FCSTD DOCUMENT  (FreeCAD 0.16R6223 (Git))
Label: map2_smd_assy
License: All rights reserved
LicenseURL: http://en.wikipedia.org/wiki/All_rights_reserved
objects: Part::Feature×12, Part::FeaturePython×7, Sketcher::SketchObject×2, PartDesign::Pad×2, Part::MultiFuse×2
note: 27 computed .brp shape members not serialized (recipe doc carries the construction recipe); baked Part::Feature solids carry a one-line shape summary decoded from their .brp

FEATURE [Sketcher::SketchObject] Sketch
  sketch-geometry (4):
    g0: LineSegment StartX=0 StartY=0 StartZ=0 EndX=132.08 EndY=0 EndZ=0
    g1: LineSegment StartX=132.08 StartY=0 StartZ=0 EndX=132.08 EndY=127 EndZ=0
    g2: LineSegment StartX=132.08 StartY=127 StartZ=0 EndX=0 EndY=127 EndZ=0
    g3: LineSegment StartX=0 StartY=127 StartZ=0 EndX=0 EndY=0 EndZ=0
  constraints (11):
    c: Coincident(g0,g1)
    c: Coincident(g1,g2)
    c: Coincident(g2,g3)
    c: Coincident(g3,g0)
    c: Horizontal(g0)
    c: Horizontal(g2)
    c: Vertical(g1)
    c: Vertical(g3)
    c: DistanceX(g2) = -132.08
    c: DistanceY(g3) = -127
    c: Coincident(g0,g-1)
FEATURE [PartDesign::Pad] Pad
  Length = 6.35
  Length2 = 100
  Reversed = true
  Sketch = -> Sketch
  Type = 0
FEATURE [Sketcher::SketchObject] Sketch001
  sketch-geometry (4):
    g0: LineSegment StartX=1.27 StartY=127 StartZ=0 EndX=6.35 EndY=127 EndZ=0
    g1: LineSegment StartX=6.35 StartY=127 StartZ=0 EndX=6.35 EndY=0 EndZ=0
    g2: LineSegment StartX=6.35 StartY=0 StartZ=0 EndX=1.27 EndY=0 EndZ=0
    g3: LineSegment StartX=1.27 StartY=0 StartZ=0 EndX=1.27 EndY=127 EndZ=0
  constraints (12):
    c: Coincident(g0,g1)
    c: Coincident(g1,g2)
    c: Coincident(g2,g3)
    c: Coincident(g3,g0)
    c: Horizontal(g0)
    c: Horizontal(g2)
    c: Vertical(g1)
    c: Vertical(g3)
    c: DistanceY(g3) = 127
    c: DistanceX(g0) = 5.08
    c: DistanceY(g-1,g2) = 0
    c: DistanceX(g-1,g2) = 1.27
FEATURE [PartDesign::Pad] Pad001
  Length = 0.254
  Length2 = 100
  Sketch = -> Sketch001
  Type = 0
FEATURE [Part::FeaturePython] Array  # Draft array (typed FeaturePython)
  Angle = 360
  ArrayType = 0
  Axis = (0,0,1)
  Base = -> Pad001
  Center = (0,0,0)
  Fuse = false
  IntervalAxis = (0,0,0)
  IntervalX = (25.4,0,0)
  IntervalY = (0,0,0)
  IntervalZ = (0,0,0)
  NumberPolar = 1
  NumberX = 6
  NumberY = 2
  NumberZ = 1
  Placement = pos=(2.54,0,0) rot=(0,0,1;0rad)
FEATURE [Part::Feature] Pcb
  Placement = pos=(-45.72,45.72,0) rot=(0,0,1;0rad)
  shape: bbox 25.4 x 25.4 x 1.6 mm, 76 faces (baked)
FEATURE [Part::Feature] Shape  label="R_photo_"
  Placement = pos=(0,-1.27,0) rot=(0,0,-1;1.5708rad)
  shape: bbox 4.775 x 5.625 x 3.889 mm, 86 faces (baked)
FEATURE [Part::Feature] Shape001  label="Fusion_"
  Placement = pos=(0,5.715,0) rot=(0,0,-1;1.5708rad)
  shape: bbox 6.02 x 5.42 x 14.8 mm, 87 faces (baked)
FEATURE [Part::Feature] Shape002  label="Tr_SOT23_"
  Placement = pos=(-8.382,9.906,0) rot=(0,0,1;3.14159rad)
  shape: bbox 2.9 x 2.3 x 1 mm, 217 faces (baked)
FEATURE [Part::Feature] Shape003  label="r_0805_"
  Placement = pos=(0,-6.35,0) rot=(0,0,1;3.14159rad)
  shape: bbox 2 x 1.25 x 0.782 mm, 90 faces (baked)
FEATURE [Part::Feature] Shape004  label="r_0805_001"
  Placement = pos=(4.445,3.81,0) rot=(0,0,-1;1.5708rad)
  shape: bbox 1.25 x 2 x 0.782 mm, 90 faces (baked)
FEATURE [Part::Feature] Shape005  label="r_0805_002"
  Placement = pos=(0,10.16,0) rot=(0,0,1;0rad)
  shape: bbox 2 x 1.25 x 0.782 mm, 90 faces (baked)
FEATURE [Part::Feature] Shape006  label="r_0805_003"
  Placement = pos=(-4.445,3.81,0) rot=(0,0,-1;1.5708rad)
  shape: bbox 1.25 x 2 x 0.782 mm, 90 faces (baked)
FEATURE [Part::Feature] Shape007  label="cap_1210_3225M_"
  Placement = pos=(-8.255,-2.54,0) rot=(0,0,1;3.14159rad)
  shape: bbox 4.001 x 2.489 x 1.704 mm, 108 faces (baked)
FEATURE [Part::Feature] Shape008  label="cap_1210_3225M_001"
  Placement = pos=(8.255,-2.54,0) rot=(0,0,1;3.14159rad)
  shape: bbox 4.001 x 2.489 x 1.704 mm, 108 faces (baked)
FEATURE [Part::Feature] Shape009  label="cap_1210_3225M_002"
  Placement = pos=(8.89,8.89,0) rot=(0,0,1;3.14159rad)
  shape: bbox 4.001 x 2.489 x 1.704 mm, 108 faces (baked)
FEATURE [Part::MultiFuse] Fusion
  Shapes = -> [Shape,Shape001,Shape002,Shape003,Shape004,Shape005,Shape006,Shape007,Shape008,Shape009,Pcb]
FEATURE [Part::Feature] Part__Feature_solid  label="header_1x2_TH_2_54mm078 (Solid)"
  shape: bbox 2.54 x 5.08 x 12.7 mm, 78 faces (baked)
FEATURE [Part::FeaturePython] Clone  label="Clone of header_1x2_TH_2_54mm078 (Solid)"  # Draft clone (typed FeaturePython)
  Objects = -> [Part__Feature_solid]
  Placement = pos=(-25.4,0,0) rot=(0,0,1;0rad)
  Scale = (1,1,1)
FEATURE [Part::MultiFuse] Fusion001
  Placement = pos=(19.05,25.4,11.43) rot=(0,0,1;0rad)
  Shapes = -> [Fusion,Part__Feature_solid,Clone]
FEATURE [Part::FeaturePython] Array001  # Draft array (typed FeaturePython)
  Angle = 360
  ArrayType = 0
  Axis = (0,0,1)
  Base = -> Fusion001
  Center = (0,0,0)
  Fuse = false
  IntervalAxis = (0,0,0)
  IntervalX = (0,0,0)
  IntervalY = (0,25.4,0)
  IntervalZ = (0,0,0)
  NumberPolar = 1
  NumberX = 1
  NumberY = 4
  NumberZ = 1
FEATURE [Part::FeaturePython] Clone001  label="Clone of Array001"  # Draft clone (typed FeaturePython)
  Objects = -> [Array001]
  Placement = pos=(63.5,127,0) rot=(0,0,1;3.14159rad)
  Scale = (1,1,1)
FEATURE [Part::FeaturePython] Clone002  label="Clone of Array002"  # Draft clone (typed FeaturePython)
  Objects = -> [Array001]
  Placement = pos=(50.8,0,0) rot=(0,0,1;0rad)
  Scale = (1,1,1)
FEATURE [Part::FeaturePython] Clone003  label="Clone of Clone of Array001"  # Draft clone (typed FeaturePython)
  Objects = -> [Clone001]
  Placement = pos=(114.3,127,0) rot=(0,0,1;3.14159rad)
  Scale = (1,1,1)
FEATURE [Part::FeaturePython] Clone004  label="Clone of Array003"  # Draft clone (typed FeaturePython)
  Objects = -> [Array001]
  Placement = pos=(101.6,0,0) rot=(0,0,1;0rad)
  Scale = (1,1,1)
